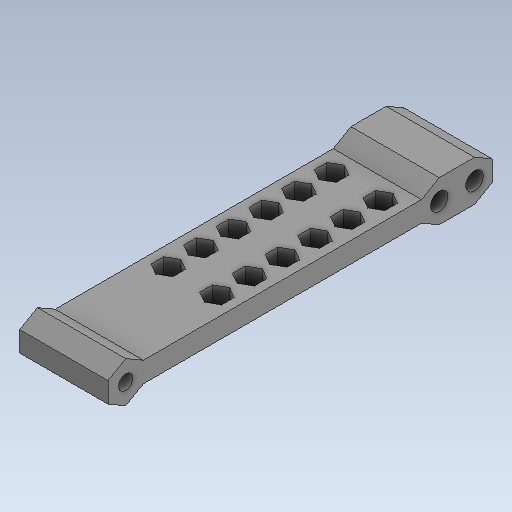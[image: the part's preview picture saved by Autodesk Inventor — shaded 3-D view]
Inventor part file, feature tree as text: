
AUTODESK INVENTOR PART (.ipt)
format: ipt  version: 2020 (Build 240168000, 168)  size: 388,096 bytes
history: native  units: in
note: dims shown in document units (in); Inventor stores cm internally (conversion verified against a paired STEP export)
features: sketch x6, extrude x5, projected_geometry x3, plane x2, mirror x1
ambient origin geometry x8: Origin, YZ Plane, XZ Plane, XY Plane, X Axis, Y Axis, Z Axis, Center Point
bodies: Solid1 (feature_tree)
feature tree (17):
  extrude  "Extrusion1"  Depth=3.4256in
  plane  "Work Plane1"
  extrude  "Extrusion2"  Depth=0.7874in
  sketch  "Sketch4"  dims[d4=0.0in d5=0.0827in]
  extrude  "Extrusion4"  Depth=0.0827in
  plane  "Work Plane2"
  extrude  "Extrusion6"  Depth=3.1106in
  mirror  "Mirror2"
  extrude  "Extrusion7"  Depth=0.315in
  sketch  "Sketch1"  dims[d0=0.1818in d1=3.4256in]
  sketch  "Sketch2"  dims[d2=0.1299in d3=0.7874in]
  sketch  "Sketch5"  dims[d6=0.7874in d7=0.0in d28=3.1106in]
  sketch  "Sketch7"  dims[d29=0.315in d31=0.315in]
  projected_geometry  "Projected Loop7"
  projected_geometry  "Projected Loop8"
  sketch  "Sketch8"  dims[d33=0.1575in d34=0.2362in d35=0.0in d38=0.315in d39=0.2756in d40=-0.3092in d41=0.0787in d42=0.0787in d43=0.0787in d44=2.3622in d46=0.2913in d47=0.3937in d49=0.3937in d51=2.3622in d53=0.2913in d54=0.3937in d56=0.3937in d58=0.0in d59=0.0in]
  projected_geometry  "Projected Loop9"
